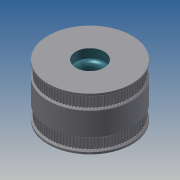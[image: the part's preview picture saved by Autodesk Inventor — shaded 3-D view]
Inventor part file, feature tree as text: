
AUTODESK INVENTOR PART (.ipt)
format: ipt  version: 2013 (Build 170138000, 138)  size: 819,712 bytes
history: native  units: mm
features: extrude x4, sketch x4, other x3, fillet x2
ambient origin geometry x8: Origin, YZ Plane, XZ Plane, XY Plane, X Axis, Y Axis, Z Axis, Center Point
bodies: Solid1 (feature_tree)
feature tree (13):
  other  "z idler pulley 2.iam"
  other  "100 pulley blank.ipt:1"
  other  "100 pulley blank.ipt:2"
  extrude  "Extrusion1"  Depth=10.0mm TaperAngle=0.0deg
  extrude  "Extrusion2"  Depth=10.0mm TaperAngle=0.0deg
  extrude  "Extrusion3"  Depth=7.0mm TaperAngle=0.0deg
  extrude  "Extrusion4"  Depth=7.0mm TaperAngle=0.0deg
  fillet  "Fillet1"  Radius=3.5mm
  fillet  "Fillet2"  Radius=3.5mm
  sketch  "Sketch1"  dims[d0=10.0mm d1=10.0mm d2=0.0mm]
  sketch  "Sketch2"  dims[d3=15.0mm d5=10.0mm d6=0.0mm]
  sketch  "Sketch3"  dims[d7=22.0mm d9=7.0mm d10=0.0mm]
  sketch  "Sketch4"  dims[d11=22.0mm d13=7.0mm d14=0.0mm d15=3.5mm d16=3.5mm]
